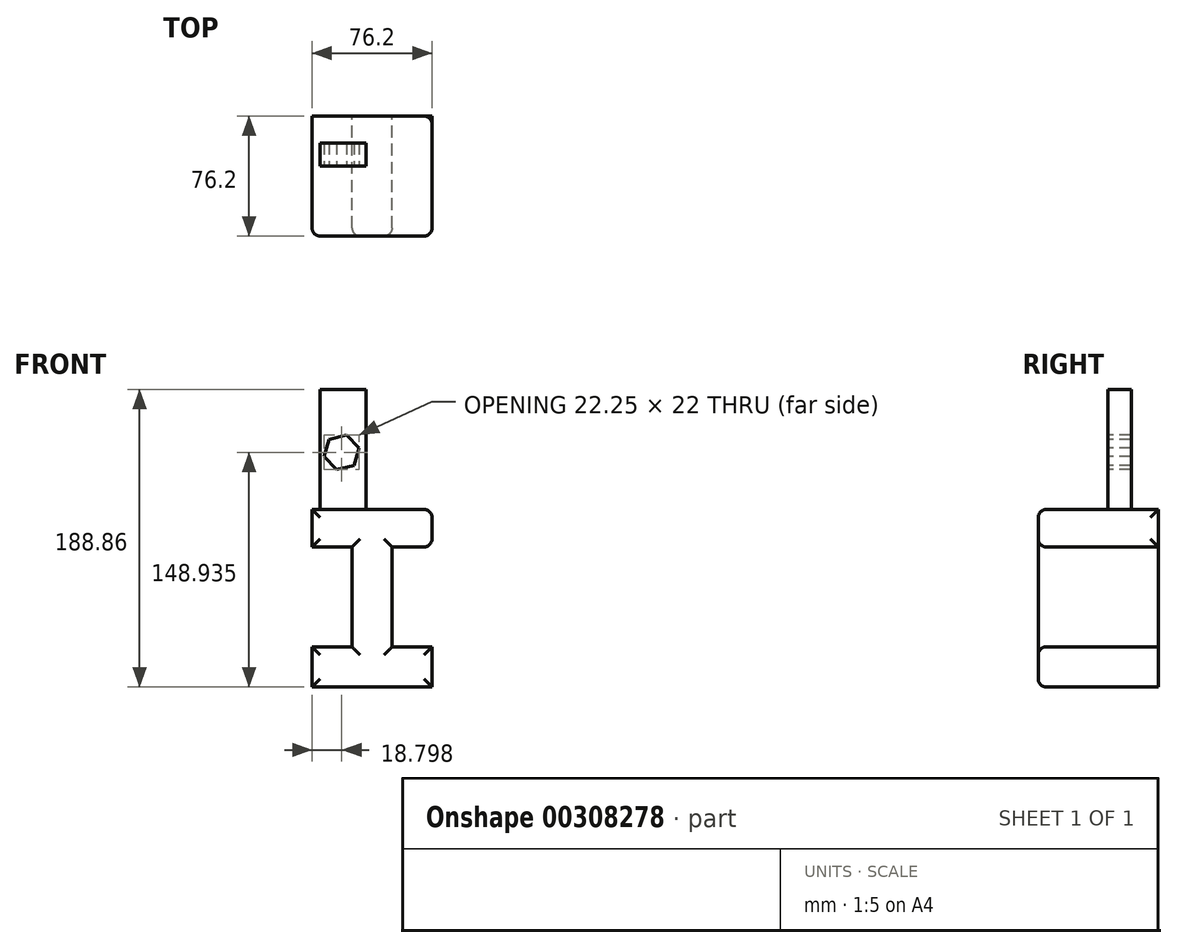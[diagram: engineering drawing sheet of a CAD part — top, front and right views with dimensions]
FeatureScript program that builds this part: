
annotation { "Feature Type Name" : "Feature", "Feature Type Description" : "" }
export const myFeature = defineFeature(function(context is Context, id is Id, definition is map)
    precondition{}
    {
        {
            var Q0;
            Q0=qCreatedBy(makeId("Front.planeOp"),FACE);
            var sketch = newSketch(context, id + "F0", { "sketchPlane" : qUnion([Q0])});
            skLineSegment(sketch, "E0", {"start": v(-39.52, -44.84) * mm, "end": v(36.68, -44.84) * mm});
            skLineSegment(sketch, "E1", {"start": v(36.68, -44.84) * mm, "end": v(36.68, -19.44) * mm});
            skLineSegment(sketch, "E2", {"start": v(36.68, -19.44) * mm, "end": v(11.28, -19.44) * mm});
            skLineSegment(sketch, "E3", {"start": v(11.28, -19.44) * mm, "end": v(11.28, 44.06) * mm});
            skLineSegment(sketch, "E4", {"start": v(11.28, 44.06) * mm, "end": v(36.68, 44.06) * mm});
            skLineSegment(sketch, "E5", {"start": v(36.68, 44.06) * mm, "end": v(36.68, 67.82) * mm});
            skLineSegment(sketch, "E6", {"start": v(36.68, 67.82) * mm, "end": v(-39.52, 67.82) * mm});
            skLineSegment(sketch, "E7", {"start": v(-39.52, 67.82) * mm, "end": v(-39.52, 44.06) * mm});
            skLineSegment(sketch, "E8", {"start": v(-39.52, 44.06) * mm, "end": v(-14.12, 44.06) * mm});
            skLineSegment(sketch, "E9", {"start": v(-14.12, 44.06) * mm, "end": v(-14.12, -19.44) * mm});
            skLineSegment(sketch, "E10", {"start": v(-14.12, -19.44) * mm, "end": v(-39.52, -19.44) * mm});
            skLineSegment(sketch, "E11", {"start": v(-39.52, -19.44) * mm, "end": v(-39.52, -44.84) * mm});
            skSolve(sketch);
        }
        {
            var Q0;
            Q0=makeQuery(id+"F0.imprint","IMPRINT",FACE,{"disambiguationData":[TD([[makeQuery(id+"F0.imprint","IMPRINT",EDGE,{"derivedFrom":sQuery(id+"F0.wireOp",EDGE,"E0")}),1.0]])]});
            extrude(context, id + "F1", {"entities" : qUnion([Q0]), "depth" : 76.2 * mm});
        }
        {
            var Q0;
            Q0=makeQuery(id+"F1.opExtrude","SWEPT_FACE",FACE,{"disambiguationData":[OSD([sQuery(id+"F0.wireOp",EDGE,"E6")])]});
            var sketch = newSketch(context, id + "F2", { "sketchPlane" : qUnion([Q0])});
            skLineSegment(sketch, "E12.bottom", {"start": v(-34.54, -17.1) * mm, "end": v(-5.23, -17.1) * mm});
            skLineSegment(sketch, "E12.top", {"start": v(-34.54, -31.85) * mm, "end": v(-5.23, -31.85) * mm});
            skLineSegment(sketch, "E12.left", {"start": v(-34.54, -17.1) * mm, "end": v(-34.54, -31.85) * mm});
            skLineSegment(sketch, "E12.right", {"start": v(-5.23, -17.1) * mm, "end": v(-5.23, -31.85) * mm});
            skSolve(sketch);
        }
        {
            var Q0;
            Q0=makeQuery(id+"F2.imprint","IMPRINT",FACE,{"disambiguationData":[TD([[makeQuery(id+"F2.imprint","IMPRINT",EDGE,{"derivedFrom":sQuery(id+"F2.wireOp",EDGE,"E12.bottom")}),-1.0]])]});
            extrude(context, id + "F3", {"entities" : qUnion([Q0]), "operationType" : NewBodyOperationType.ADD, "depth" : 76.2 * mm});
        }
        {
            var Q0;
            Q0=makeQuery(id+"F3.opExtrude","SWEPT_FACE",FACE,{"disambiguationData":[OSD([sQuery(id+"F2.wireOp",EDGE,"E12.top")])]});
            var sketch = newSketch(context, id + "F4", { "sketchPlane" : qUnion([Q0])});
            skCircle(sketch, "E13.cCircle", {"center": v(-20.72, 104.1) * mm, "radius": 9.92 * mm, "construction": true});
            skLineSegment(sketch, "E13.0", {"start": v(-28.65, 112.36) * mm, "end": v(-17.53, 115.1) * mm});
            skLineSegment(sketch, "E13.1", {"start": v(-17.53, 115.1) * mm, "end": v(-9.6, 106.83) * mm});
            skLineSegment(sketch, "E13.2", {"start": v(-9.6, 106.83) * mm, "end": v(-12.8, 95.83) * mm});
            skLineSegment(sketch, "E13.3", {"start": v(-12.8, 95.83) * mm, "end": v(-23.92, 93.1) * mm});
            skLineSegment(sketch, "E13.4", {"start": v(-23.92, 93.1) * mm, "end": v(-31.85, 101.36) * mm});
            skLineSegment(sketch, "E13.5", {"start": v(-31.85, 101.36) * mm, "end": v(-28.65, 112.36) * mm});
            skPoint(sketch, "E13.0.midPoint", {"position": v(-23.09, 113.73) * mm});
            skSolve(sketch);
        }
        {
            var Q0;
            Q0=makeQuery(id+"F4.imprint","IMPRINT",FACE,{"disambiguationData":[TD([[makeQuery(id+"F4.imprint","IMPRINT",EDGE,{"derivedFrom":sQuery(id+"F4.wireOp",EDGE,"E13.0")}),-1.0]])]});
            extrude(context, id + "F5", {"entities" : qUnion([Q0]), "operationType" : NewBodyOperationType.REMOVE, "endBound" : BoundingType.THROUGH_ALL, "oppositeDirection" : true, "depth" : 25.4 * mm});
        }
        {
            var Q0;
            Q0=makeQuery(id+"F1.opExtrude","CAP_EDGE",EDGE,{"disambiguationData":[OSD([sQuery(id+"F0.wireOp",EDGE,"E6")])],"isStart":false});
            var Q1;
            Q1=makeQuery(id+"F1.opExtrude","SWEPT_EDGE",EDGE,{"disambiguationData":[OSD([sQuery(id+"F0.wireOp",EDGE,"E5"),sQuery(id+"F0.wireOp",EDGE,"E6")])]});
            var Q2;
            Q2=makeQuery(id+"F1.opExtrude","SWEPT_FACE",FACE,{"disambiguationData":[OSD([sQuery(id+"F0.wireOp",EDGE,"E5")])]});
            var Q3;
            Q3=makeQuery(id+"F1.opExtrude","CAP_FACE",FACE,{"disambiguationData":[OSD([sQuery(id+"F0.wireOp",EDGE,"E0"),sQuery(id+"F0.wireOp",EDGE,"E1"),sQuery(id+"F0.wireOp",EDGE,"E2"),sQuery(id+"F0.wireOp",EDGE,"E3"),sQuery(id+"F0.wireOp",EDGE,"E4"),sQuery(id+"F0.wireOp",EDGE,"E5"),sQuery(id+"F0.wireOp",EDGE,"E6"),sQuery(id+"F0.wireOp",EDGE,"E7"),sQuery(id+"F0.wireOp",EDGE,"E8"),sQuery(id+"F0.wireOp",EDGE,"E9"),sQuery(id+"F0.wireOp",EDGE,"E10"),sQuery(id+"F0.wireOp",EDGE,"E11")])],"isStart":false});
            fillet(context, id + "F6", {"entities" : qUnion([Q0, Q1, Q2, Q3]), "radius" : 5.08 * mm, "tangentPropagation" : true, "allowEdgeOverflow" : false});
        }
    });
